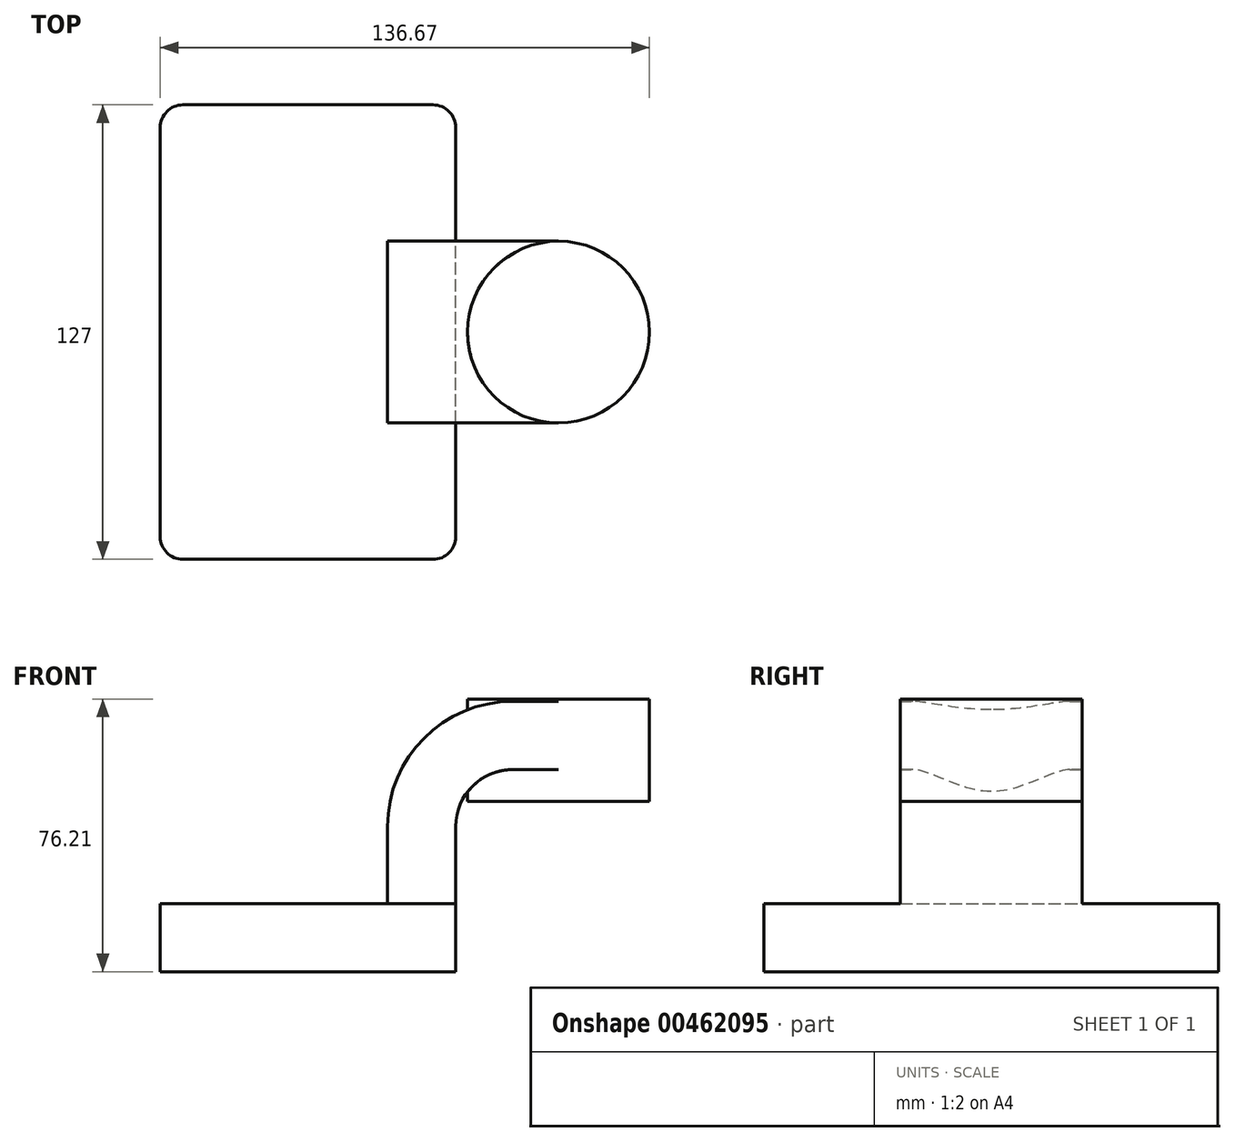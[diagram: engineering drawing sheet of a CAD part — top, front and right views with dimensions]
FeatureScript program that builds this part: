
annotation { "Feature Type Name" : "Feature", "Feature Type Description" : "" }
export const myFeature = defineFeature(function(context is Context, id is Id, definition is map)
    precondition{}
    {
        {
            var Q0;
            Q0=qCreatedBy(makeId("Front.planeOp"),FACE);
            var sketch = newSketch(context, id + "F0", { "sketchPlane" : qUnion([Q0])});
            skLineSegment(sketch, "E0.bottom", {"start": v(41.28, -9.52) * mm, "end": v(-41.28, -9.53) * mm});
            skLineSegment(sketch, "E0.top", {"start": v(41.28, 9.53) * mm, "end": v(-41.28, 9.53) * mm});
            skLineSegment(sketch, "E0.left", {"start": v(41.28, -9.52) * mm, "end": v(41.28, 9.53) * mm});
            skLineSegment(sketch, "E0.right", {"start": v(-41.28, -9.53) * mm, "end": v(-41.28, 9.53) * mm});
            skPoint(sketch, "E0.middle", {"position": v(0, 0) * mm});
            skLineSegment(sketch, "E1.bottom", {"start": v(120.8, 38.1) * mm, "end": v(70, 38.1) * mm});
            skLineSegment(sketch, "E1.top", {"start": v(120.8, 66.68) * mm, "end": v(70, 66.68) * mm});
            skLineSegment(sketch, "E1.left", {"start": v(120.8, 38.1) * mm, "end": v(120.8, 66.67) * mm});
            skLineSegment(sketch, "E1.right", {"start": v(70, 38.1) * mm, "end": v(70, 66.67) * mm});
            skPoint(sketch, "E1.middle", {"position": v(95.4, 52.39) * mm});
            skLineSegment(sketch, "E2", {"start": v(41.28, 9.53) * mm, "end": v(41.28, 31.06) * mm});
            skArc(sketch, "E3", {"start": v(41.27, 31.06) * mm, "mid": v(45.92, 42.28) * mm, "end": v(57.15, 46.93) * mm});
            skLineSegment(sketch, "E4", {"start": v(57.15, 46.93) * mm, "end": v(70, 46.93) * mm});
            skLineSegment(sketch, "E5.0", {"start": v(57.15, 65.98) * mm, "end": v(85.44, 65.98) * mm});
            skArc(sketch, "E5.1", {"start": v(22.23, 31.06) * mm, "mid": v(32.45, 55.75) * mm, "end": v(57.15, 65.98) * mm});
            skLineSegment(sketch, "E5.2", {"start": v(22.22, 9.53) * mm, "end": v(22.22, 31.06) * mm});
            skFitSpline(sketch, "E6", {"points": [v(-41.28, 9.53) * mm, v(57.15, 65.98) * mm], "startDerivative": vector(43.85, 93.7) * mm, "endDerivative": vector(140.38, -3) * mm});
            skLineSegment(sketch, "E7", {"start": v(95.4, 66.68) * mm, "end": v(95.4, 38.1) * mm});
            skSolve(sketch);
        }
        {
            var Q0;
            Q0=makeQuery(id+"F0.imprint","IMPRINT",FACE,{"disambiguationData":[TD([[makeQuery(id+"F0.imprint","IMPRINT",EDGE,{"derivedFrom":sQuery(id+"F0.wireOp",EDGE,"E0.bottom")}),-1.0]])]});
            extrude(context, id + "F1", {"entities" : qUnion([Q0]), "endBound" : BoundingType.SYMMETRIC, "depth" : 127 * mm});
        }
        {
            var Q0;
            {var subQ0=sQuery(id+"F0.wireOp",EDGE,"E2");Q0=makeQuery(id+"F0.imprint","IMPRINT",FACE,{"disambiguationData":[TD([[makeQuery(id+"F0.imprint","IMPRINT",EDGE,{"derivedFrom":subQ0}),1.0]])]});}
            extrude(context, id + "F2", {"entities" : qUnion([Q0]), "operationType" : NewBodyOperationType.ADD, "endBound" : BoundingType.SYMMETRIC, "depth" : 50.8 * mm});
        }
        {
            var Q0;
            Q0=makeQuery(id+"F0.imprint","IMPRINT",FACE,{"disambiguationData":[TD([[makeQuery(id+"F0.imprint","IMPRINT",EDGE,{"derivedFrom":sQuery(id+"F0.wireOp",EDGE,"E5.1")}),1.0]])]});
            extrude(context, id + "F3", {"entities" : qUnion([Q0]), "operationType" : NewBodyOperationType.ADD, "depth" : 15.88 * mm});
        }
        {
            var Q0;
            {var subQ6=sQuery(id+"F0.wireOp",EDGE,"E7");Q0=makeQuery(id+"F0.imprint","IMPRINT",FACE,{"disambiguationData":[TD([[makeQuery(id+"F0.imprint","IMPRINT",EDGE,{"derivedFrom":subQ6}),-1.0]])]});}
            var Q1;
            Q1=sQuery(id+"F0.wireOp",EDGE,"E1.right");
            revolve(context, id + "F4", {"operationType" : NewBodyOperationType.ADD, "entities" : qUnion([Q0]), "axis" : qUnion([Q1]), "revolveType" : RevolveType.FULL});
        }
        {
            var Q0;
            Q0=makeQuery(id+"F1.opExtrude","CAP_EDGE",EDGE,{"disambiguationData":[OSD([sQuery(id+"F0.wireOp",EDGE,"E0.right")])],"isStart":false});
            var Q1;
            Q1=makeQuery(id+"F1.opExtrude","CAP_EDGE",EDGE,{"disambiguationData":[OSD([sQuery(id+"F0.wireOp",EDGE,"E0.left")])],"isStart":false});
            var Q2;
            Q2=makeQuery(id+"F1.opExtrude","CAP_EDGE",EDGE,{"disambiguationData":[OSD([sQuery(id+"F0.wireOp",EDGE,"E0.right")])],"isStart":true});
            var Q3;
            Q3=makeQuery(id+"F1.opExtrude","CAP_EDGE",EDGE,{"disambiguationData":[OSD([sQuery(id+"F0.wireOp",EDGE,"E0.left")])],"isStart":true});
            fillet(context, id + "F5", {"entities" : qUnion([Q0, Q1, Q2, Q3]), "radius" : 6.35 * mm, "tangentPropagation" : true, "allowEdgeOverflow" : false});
        }
    });
